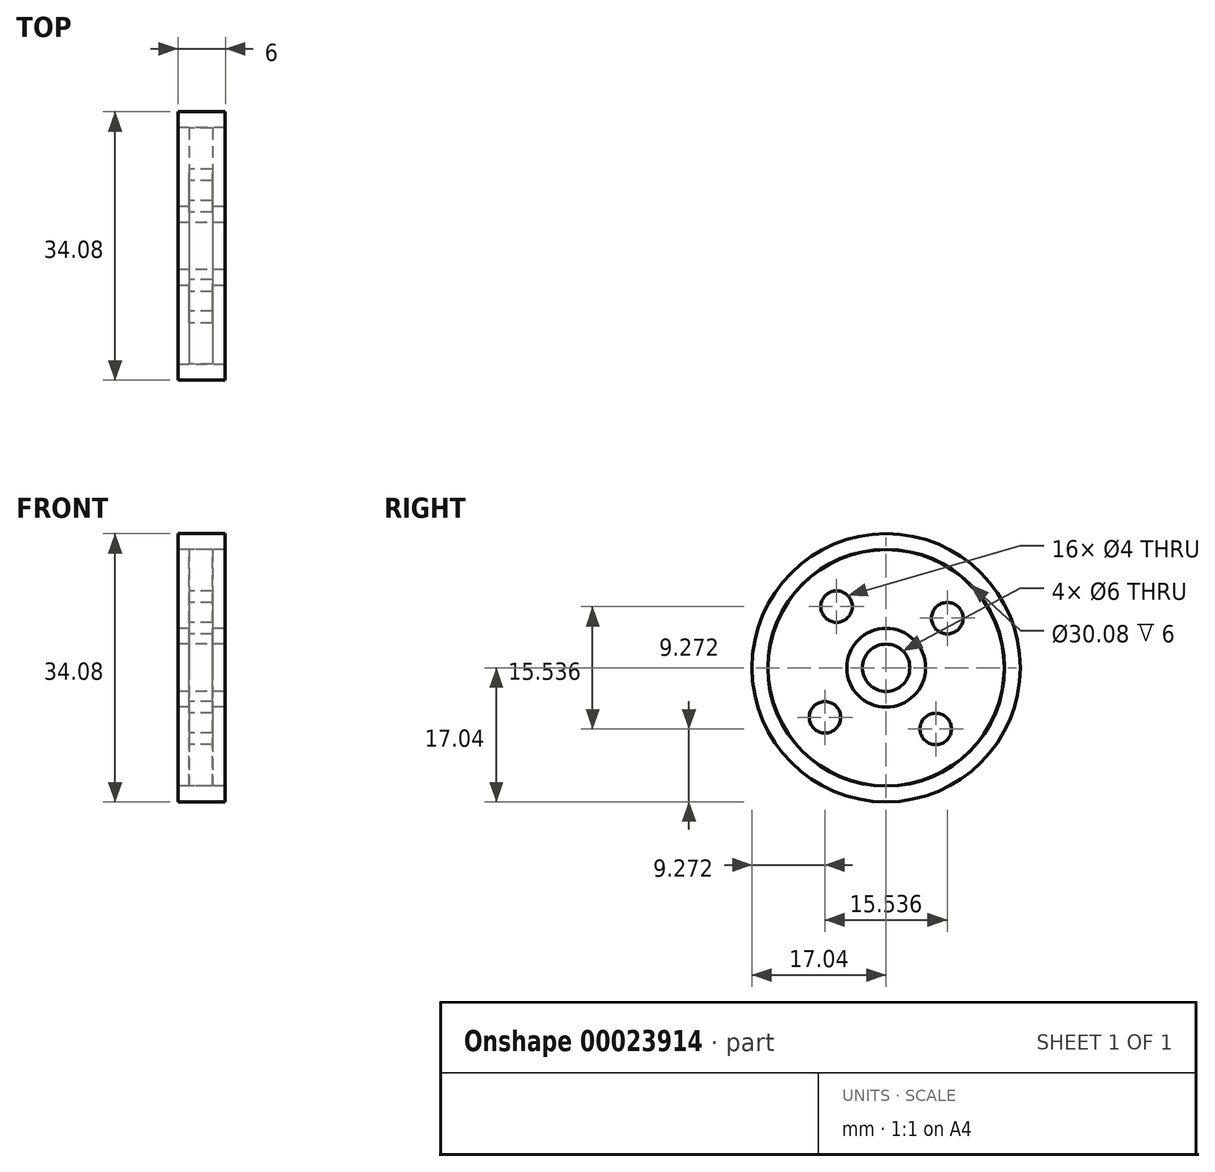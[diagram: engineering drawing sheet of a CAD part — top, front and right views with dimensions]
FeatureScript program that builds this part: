
annotation { "Feature Type Name" : "Feature", "Feature Type Description" : "" }
export const myFeature = defineFeature(function(context is Context, id is Id, definition is map)
    precondition{}
    {
        {
            var Q0;
            Q0=qCreatedBy(makeId("Top.planeOp"),FACE);
            var sketch = newSketch(context, id + "F0", { "sketchPlane" : qUnion([Q0])});
            skLineSegment(sketch, "E0", {"start": v(-22.71, 0) * mm, "end": v(23.15, 0) * mm, "construction": true});
            skLineSegment(sketch, "E1.bottom", {"start": v(-2.83, 5) * mm, "end": v(3.17, 5) * mm});
            skLineSegment(sketch, "E1.top", {"start": v(-2.83, 3) * mm, "end": v(3.17, 3) * mm});
            skLineSegment(sketch, "E1.left", {"start": v(-2.83, 5) * mm, "end": v(-2.83, 3) * mm});
            skLineSegment(sketch, "E1.right", {"start": v(3.17, 5) * mm, "end": v(3.17, 3) * mm});
            skLineSegment(sketch, "E2.bottom", {"start": v(-1.45, 5) * mm, "end": v(1.55, 5) * mm});
            skLineSegment(sketch, "E2.top", {"start": v(-1.45, 15) * mm, "end": v(1.55, 15) * mm});
            skLineSegment(sketch, "E2.left", {"start": v(-1.45, 5) * mm, "end": v(-1.45, 15) * mm});
            skLineSegment(sketch, "E2.right", {"start": v(1.55, 5) * mm, "end": v(1.55, 15) * mm});
            skLineSegment(sketch, "E3.bottom", {"start": v(-2.83, 15.04) * mm, "end": v(3.17, 15.04) * mm});
            skLineSegment(sketch, "E3.top", {"start": v(-2.83, 17.04) * mm, "end": v(3.17, 17.04) * mm});
            skLineSegment(sketch, "E3.left", {"start": v(-2.83, 15.04) * mm, "end": v(-2.83, 17.04) * mm});
            skLineSegment(sketch, "E3.right", {"start": v(3.17, 15.04) * mm, "end": v(3.17, 17.04) * mm});
            skSolve(sketch);
        }
        {
            var Q0;
            Q0 = qSketchRegion(id + "F0", true);
            var Q1;
            Q1=sQuery(id+"F0.wireOp",EDGE,"E0");
            revolve(context, id + "F1", {"entities" : qUnion([Q0]), "axis" : qUnion([Q1]), "revolveType" : RevolveType.FULL});
        }
        {
            var Q0;
            Q0=makeQuery(id+"F1.opRevolve","SWEPT_FACE",FACE,{"disambiguationData":[OSD([sQuery(id+"F0.wireOp",EDGE,"E2.left")])]});
            var sketch = newSketch(context, id + "F2", { "sketchPlane" : qUnion([Q0])});
            skSolve(sketch);
        }
        {
            var Q0;
            Q0=makeQuery(id+"F1.opRevolve","SWEPT_BODY",BODY,{"disambiguationData":[OSD([sQuery(id+"F0.wireOp",EDGE,"E1.bottom"),sQuery(id+"F0.wireOp",EDGE,"E1.top"),sQuery(id+"F0.wireOp",EDGE,"E1.left"),sQuery(id+"F0.wireOp",EDGE,"E1.right"),sQuery(id+"F0.wireOp",EDGE,"E2.top"),sQuery(id+"F0.wireOp",EDGE,"E2.left"),sQuery(id+"F0.wireOp",EDGE,"E2.right")])]});
            var Q1;
            Q1=makeQuery(id+"F1.opRevolve","SWEPT_EDGE",EDGE,{"disambiguationData":[OSD([sQuery(id+"F0.wireOp",EDGE,"E1.top"),sQuery(id+"F0.wireOp",EDGE,"E1.left")])]});
            circularPattern(context, id + "F3", {"entities" : qUnion([Q0]), "axis" : qUnion([Q1]), "angle" : 90 * degree, "instanceCount" : 4});
        }
        {
            var Q0;
            {var subQ0=sQuery(id+"F0.wireOp",EDGE,"E2.left");Q0=makeQuery(id+"F2.imprint","IMPRINT",FACE,{"disambiguationData":[TD([[makeQuery(id+"F2.imprint","IMPRINT",EDGE,{"derivedFrom":makeQuery(id+"F1.opRevolve","SWEPT_EDGE",EDGE,{"disambiguationData":[OSD([sQuery(id+"F0.wireOp",EDGE,"E2.top"),subQ0])]})}),1.0]])]});}
            var sketch = newSketch(context, id + "F4", { "sketchPlane" : qUnion([Q0])});
            skCircle(sketch, "E4", {"center": v(-7.77, 6.3) * mm, "radius": 2 * mm});
            skCircle(sketch, "E5", {"center": v(6.3, 7.77) * mm, "radius": 2 * mm});
            skCircle(sketch, "E6", {"center": v(7.77, -6.3) * mm, "radius": 2 * mm});
            skCircle(sketch, "E7", {"center": v(-6.3, -7.77) * mm, "radius": 2 * mm});
            skSolve(sketch);
        }
        {
            var Q0;
            Q0 = qSketchRegion(id + "F4", true);
            extrude(context, id + "F5", {"entities" : qUnion([Q0]), "operationType" : NewBodyOperationType.REMOVE, "oppositeDirection" : true, "depth" : 100 * mm});
        }
    });
